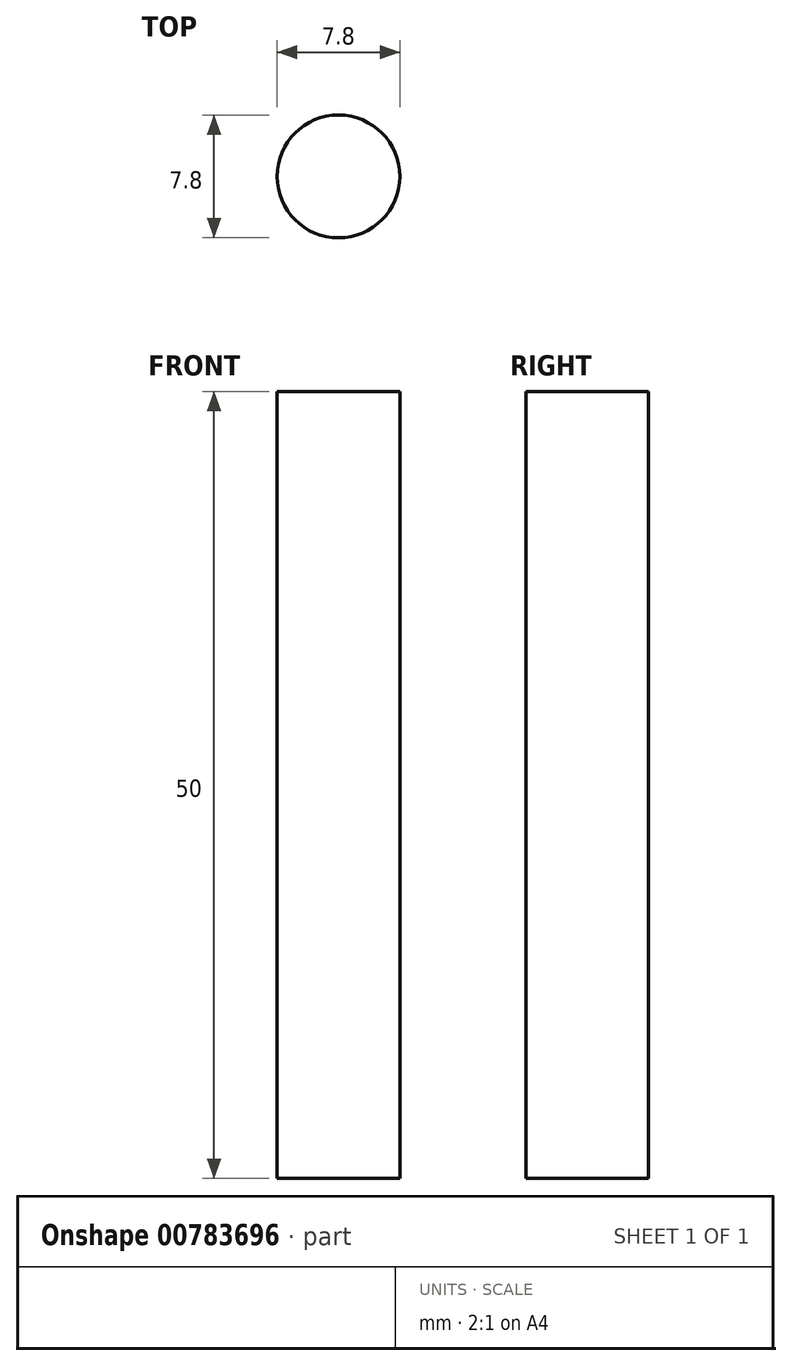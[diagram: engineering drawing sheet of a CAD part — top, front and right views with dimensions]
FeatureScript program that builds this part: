
annotation { "Feature Type Name" : "Feature", "Feature Type Description" : "" }
export const myFeature = defineFeature(function(context is Context, id is Id, definition is map)
    precondition{}
    {
        {
            var Q0;
            Q0=qCreatedBy(makeId("Top.planeOp"),FACE);
            var sketch = newSketch(context, id + "F0", { "sketchPlane" : qUnion([Q0])});
            skCircle(sketch, "E0", {"center": v(0, 0) * mm, "radius": 3.9 * mm});
            skSolve(sketch);
        }
        {
            var Q0;
            Q0=makeQuery(id+"F0.imprint","IMPRINT",FACE,{"disambiguationData":[TD([[makeQuery(id+"F0.imprint","IMPRINT",EDGE,{"derivedFrom":sQuery(id+"F0.wireOp",EDGE,"E0")}),1.0]])]});
            extrude(context, id + "F1", {"entities" : qUnion([Q0]), "depth" : 50 * mm, "offsetDistance" : 25.4 * mm});
        }
    });
